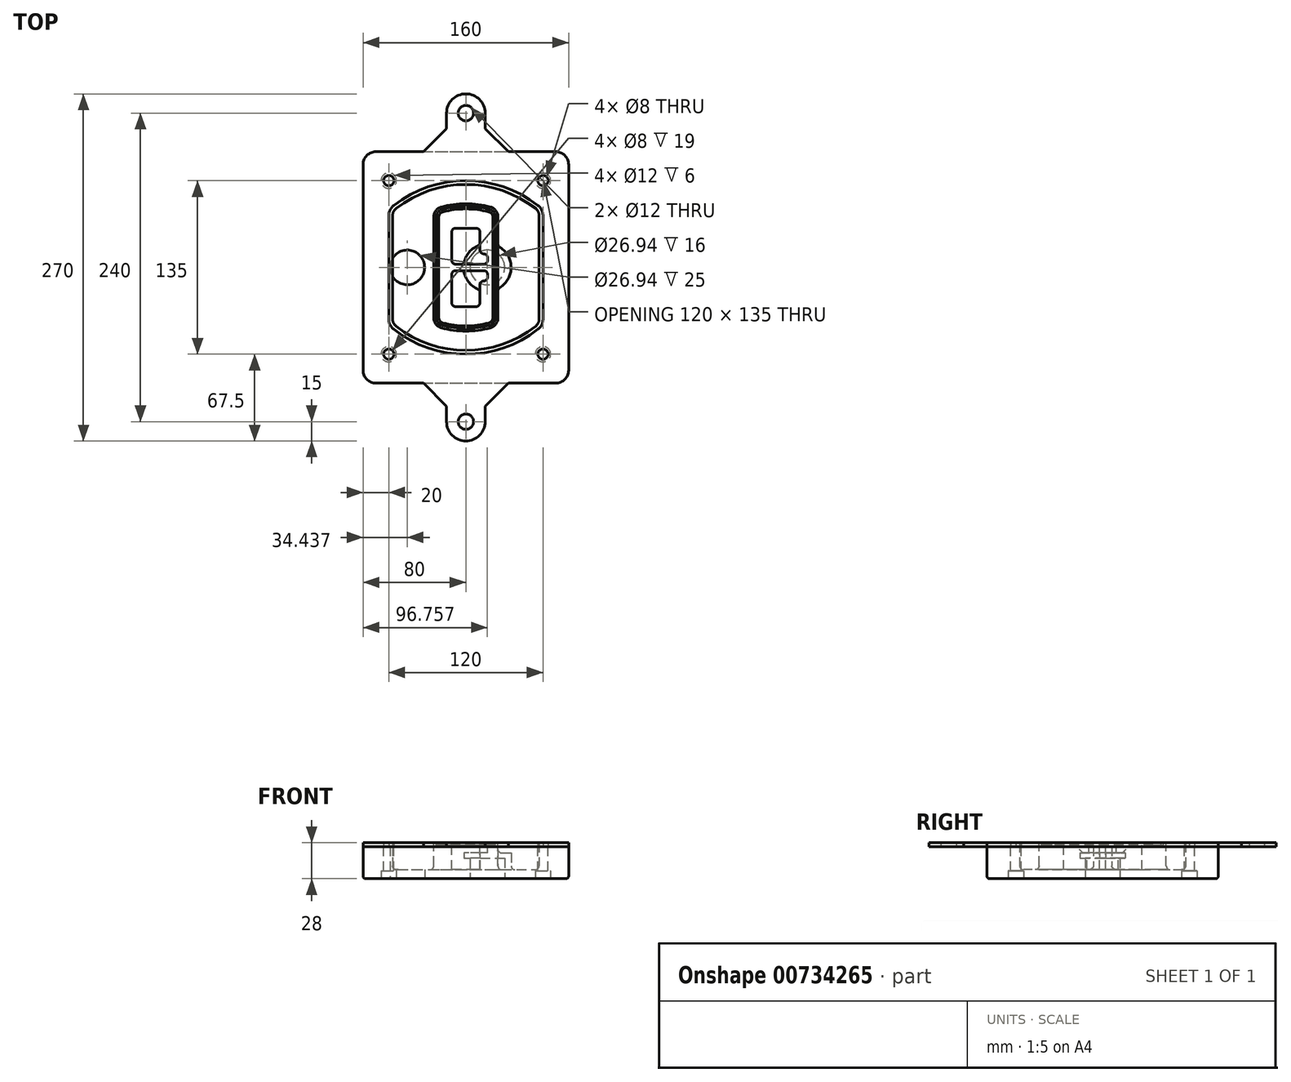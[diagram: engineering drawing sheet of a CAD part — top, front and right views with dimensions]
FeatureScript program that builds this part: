
annotation { "Feature Type Name" : "Feature", "Feature Type Description" : "" }
export const myFeature = defineFeature(function(context is Context, id is Id, definition is map)
    precondition{}
    {
        {
            var Q0;
            Q0=qCreatedBy(makeId("Top.planeOp"),FACE);
            var sketch = newSketch(context, id + "F0", { "sketchPlane" : qUnion([Q0])});
            skPoint(sketch, "E0.rect.middle", {"position": v(0, 0) * mm});
            skLineSegment(sketch, "E1.bottom", {"start": v(-70, -90) * mm, "end": v(70, -90) * mm});
            skLineSegment(sketch, "E1.top", {"start": v(-70, 90) * mm, "end": v(70, 90) * mm});
            skLineSegment(sketch, "E1.left", {"start": v(-80, -80) * mm, "end": v(-80, 80) * mm});
            skLineSegment(sketch, "E1.right", {"start": v(80, -80) * mm, "end": v(80, 80) * mm});
            skLineSegment(sketch, "E2", {"start": v(-80, 90) * mm, "end": v(80, -90) * mm, "construction": true});
            skLineSegment(sketch, "E3", {"start": v(80, 90) * mm, "end": v(-80, -90) * mm, "construction": true});
            skCircle(sketch, "E4", {"center": v(-60, 67.5) * mm, "radius": 4 * mm});
            skCircle(sketch, "E5", {"center": v(60, 67.5) * mm, "radius": 4 * mm});
            skCircle(sketch, "E6", {"center": v(60, -67.5) * mm, "radius": 4 * mm});
            skCircle(sketch, "E7", {"center": v(-60, -67.5) * mm, "radius": 4 * mm});
            skLineSegment(sketch, "E8", {"start": v(-60, 67.5) * mm, "end": v(60, 67.5) * mm, "construction": true});
            skLineSegment(sketch, "E9", {"start": v(60, 67.5) * mm, "end": v(60, -67.5) * mm, "construction": true});
            skLineSegment(sketch, "E10", {"start": v(60, -67.5) * mm, "end": v(-60, -67.5) * mm, "construction": true});
            skLineSegment(sketch, "E11", {"start": v(-60, -67.5) * mm, "end": v(-60, 67.5) * mm, "construction": true});
            skLineSegment(sketch, "E12", {"start": v(-60, 40.3) * mm, "end": v(-60, -40.3) * mm});
            skLineSegment(sketch, "E13", {"start": v(60, 40.3) * mm, "end": v(60, -40.3) * mm});
            skArc(sketch, "E14", {"start": v(56.15, 48.18) * mm, "mid": v(0, 67.5) * mm, "end": v(-56.15, 48.18) * mm});
            skArc(sketch, "E15", {"start": v(-56.15, -48.18) * mm, "mid": v(0, -67.5) * mm, "end": v(56.15, -48.18) * mm});
            skLineSegment(sketch, "E16", {"start": v(-60, 0) * mm, "end": v(60, 0) * mm, "construction": true});
            skPoint(sketch, "E17.visualSharp", {"position": v(-60, -45) * mm});
            skArc(sketch, "E17.filletArc", {"start": v(-60, -40.3) * mm, "mid": v(-58.99, -44.68) * mm, "end": v(-56.15, -48.18) * mm});
            skPoint(sketch, "E18.visualSharp", {"position": v(-60, 45) * mm});
            skArc(sketch, "E18.filletArc", {"start": v(-56.15, 48.18) * mm, "mid": v(-58.99, 44.68) * mm, "end": v(-60, 40.3) * mm});
            skPoint(sketch, "E19.visualSharp", {"position": v(60, 45) * mm});
            skArc(sketch, "E19.filletArc", {"start": v(60, 40.3) * mm, "mid": v(58.99, 44.68) * mm, "end": v(56.15, 48.18) * mm});
            skPoint(sketch, "E20.visualSharp", {"position": v(60, -45) * mm});
            skArc(sketch, "E20.filletArc", {"start": v(56.15, -48.18) * mm, "mid": v(58.99, -44.68) * mm, "end": v(60, -40.3) * mm});
            skPoint(sketch, "E21.visualSharp", {"position": v(-80, 90) * mm});
            skArc(sketch, "E21.filletArc", {"start": v(-70, 90) * mm, "mid": v(-77.07, 87.07) * mm, "end": v(-80, 80) * mm});
            skPoint(sketch, "E22.visualSharp", {"position": v(80, 90) * mm});
            skArc(sketch, "E22.filletArc", {"start": v(80, 80) * mm, "mid": v(77.07, 87.07) * mm, "end": v(70, 90) * mm});
            skPoint(sketch, "E23.visualSharp", {"position": v(80, -90) * mm});
            skArc(sketch, "E23.filletArc", {"start": v(70, -90) * mm, "mid": v(77.07, -87.07) * mm, "end": v(80, -80) * mm});
            skPoint(sketch, "E24.visualSharp", {"position": v(-80, -90) * mm});
            skArc(sketch, "E24.filletArc", {"start": v(-80, -80) * mm, "mid": v(-77.07, -87.07) * mm, "end": v(-70, -90) * mm});
            skArc(sketch, "E25.0", {"start": v(57, 40.3) * mm, "mid": v(56.3, 43.36) * mm, "end": v(54.3, 45.81) * mm});
            skLineSegment(sketch, "E25.1", {"start": v(57, 40.3) * mm, "end": v(57, -40.3) * mm});
            skArc(sketch, "E25.2", {"start": v(54.3, -45.81) * mm, "mid": v(56.3, -43.36) * mm, "end": v(57, -40.3) * mm});
            skArc(sketch, "E25.3", {"start": v(-54.3, -45.81) * mm, "mid": v(0, -64.5) * mm, "end": v(54.3, -45.81) * mm});
            skArc(sketch, "E25.4", {"start": v(-57, -40.3) * mm, "mid": v(-56.3, -43.36) * mm, "end": v(-54.3, -45.81) * mm});
            skArc(sketch, "E25.5", {"start": v(54.3, 45.81) * mm, "mid": v(0, 64.5) * mm, "end": v(-54.3, 45.81) * mm});
            skLineSegment(sketch, "E25.6", {"start": v(-57, 40.3) * mm, "end": v(-57, -40.3) * mm});
            skArc(sketch, "E25.7", {"start": v(-54.3, 45.81) * mm, "mid": v(-56.3, 43.36) * mm, "end": v(-57, 40.3) * mm});
            skArc(sketch, "E26.0", {"start": v(-58.62, 51.33) * mm, "mid": v(-62.58, 46.43) * mm, "end": v(-64, 40.3) * mm});
            skArc(sketch, "E26.1", {"start": v(58.62, 51.33) * mm, "mid": v(0, 71.5) * mm, "end": v(-58.62, 51.33) * mm});
            skArc(sketch, "E26.2", {"start": v(64, 40.3) * mm, "mid": v(62.58, 46.43) * mm, "end": v(58.62, 51.33) * mm});
            skLineSegment(sketch, "E26.3", {"start": v(64, 40.3) * mm, "end": v(64, -40.3) * mm});
            skArc(sketch, "E26.4", {"start": v(58.62, -51.33) * mm, "mid": v(62.58, -46.43) * mm, "end": v(64, -40.3) * mm});
            skLineSegment(sketch, "E26.5", {"start": v(-64, 40.3) * mm, "end": v(-64, -40.3) * mm});
            skArc(sketch, "E26.6", {"start": v(-58.62, -51.33) * mm, "mid": v(0, -71.5) * mm, "end": v(58.62, -51.33) * mm});
            skArc(sketch, "E26.7", {"start": v(-64, -40.3) * mm, "mid": v(-62.58, -46.43) * mm, "end": v(-58.62, -51.33) * mm});
            skSolve(sketch);
        }
        {
            var Q0;
            Q0=makeQuery(id+"F0.imprint","IMPRINT",FACE,{"disambiguationData":[TD([[makeQuery(id+"F0.imprint","IMPRINT",EDGE,{"derivedFrom":sQuery(id+"F0.wireOp",EDGE,"E1.bottom")}),1.0]])]});
            var Q1;
            Q1=makeQuery(id+"F0.imprint","IMPRINT",FACE,{"disambiguationData":[TD([[makeQuery(id+"F0.imprint","IMPRINT",EDGE,{"derivedFrom":sQuery(id+"F0.wireOp",EDGE,"E12")}),1.0]])]});
            var Q2;
            Q2=makeQuery(id+"F0.imprint","IMPRINT",FACE,{"disambiguationData":[TD([[makeQuery(id+"F0.imprint","IMPRINT",EDGE,{"derivedFrom":sQuery(id+"F0.wireOp",EDGE,"E25.0")}),1.0]])]});
            var Q3;
            Q3=makeQuery(id+"F0.imprint","IMPRINT",FACE,{"disambiguationData":[TD([[makeQuery(id+"F0.imprint","IMPRINT",EDGE,{"derivedFrom":sQuery(id+"F0.wireOp",EDGE,"E12")}),-1.0]])]});
            extrude(context, id + "F1", {"entities" : qUnion([Q0, Q1, Q2, Q3]), "oppositeDirection" : true, "depth" : 25 * mm});
        }
        {
            var Q0;
            Q0=makeQuery(id+"F0.imprint","IMPRINT",FACE,{"disambiguationData":[TD([[makeQuery(id+"F0.imprint","IMPRINT",EDGE,{"derivedFrom":sQuery(id+"F0.wireOp",EDGE,"E12")}),1.0]])]});
            extrude(context, id + "F2", {"entities" : qUnion([Q0]), "operationType" : NewBodyOperationType.ADD, "depth" : 3 * mm});
        }
        {
            var Q0;
            Q0=makeQuery(id+"F0.imprint","IMPRINT",FACE,{"disambiguationData":[TD([[makeQuery(id+"F0.imprint","IMPRINT",EDGE,{"derivedFrom":sQuery(id+"F0.wireOp",EDGE,"E25.0")}),1.0]])]});
            extrude(context, id + "F3", {"entities" : qUnion([Q0]), "operationType" : NewBodyOperationType.REMOVE, "oppositeDirection" : true, "depth" : 18 * mm});
        }
        {
            var Q0;
            Q0=makeQuery(id+"F2.opExtrude","CAP_FACE",FACE,{"disambiguationData":[OSD([sQuery(id+"F0.wireOp",EDGE,"E12"),sQuery(id+"F0.wireOp",EDGE,"E13"),sQuery(id+"F0.wireOp",EDGE,"E14"),sQuery(id+"F0.wireOp",EDGE,"E15"),sQuery(id+"F0.wireOp",EDGE,"E17.filletArc"),sQuery(id+"F0.wireOp",EDGE,"E18.filletArc"),sQuery(id+"F0.wireOp",EDGE,"E19.filletArc"),sQuery(id+"F0.wireOp",EDGE,"E20.filletArc"),sQuery(id+"F0.wireOp",EDGE,"E25.0"),sQuery(id+"F0.wireOp",EDGE,"E25.1"),sQuery(id+"F0.wireOp",EDGE,"E25.2"),sQuery(id+"F0.wireOp",EDGE,"E25.3"),sQuery(id+"F0.wireOp",EDGE,"E25.4"),sQuery(id+"F0.wireOp",EDGE,"E25.5"),sQuery(id+"F0.wireOp",EDGE,"E25.6"),sQuery(id+"F0.wireOp",EDGE,"E25.7")])],"isStart":false});
            var sketch = newSketch(context, id + "F4", { "sketchPlane" : qUnion([Q0])});
            skArc(sketch, "E27.0", {"start": v(-19.08, -46.97) * mm, "mid": v(0, -49.5) * mm, "end": v(19.08, -46.97) * mm});
            skArc(sketch, "E28.0", {"start": v(19.08, 46.97) * mm, "mid": v(0, 49.5) * mm, "end": v(-19.08, 46.97) * mm});
            skLineSegment(sketch, "E29", {"start": v(-25, 39.25) * mm, "end": v(-25, -39.25) * mm});
            skLineSegment(sketch, "E30", {"start": v(25, 39.25) * mm, "end": v(25, -39.25) * mm});
            skLineSegment(sketch, "E31", {"start": v(-25, 45.1) * mm, "end": v(25, 45.1) * mm, "construction": true});
            skLineSegment(sketch, "E32", {"start": v(-25, -45.1) * mm, "end": v(25, -45.1) * mm, "construction": true});
            skPoint(sketch, "E33.visualSharp", {"position": v(-25, 45.1) * mm});
            skArc(sketch, "E33.filletArc", {"start": v(-19.08, 46.97) * mm, "mid": v(-23.35, 44.11) * mm, "end": v(-25, 39.25) * mm});
            skPoint(sketch, "E34.visualSharp", {"position": v(25, 45.1) * mm});
            skArc(sketch, "E34.filletArc", {"start": v(25, 39.25) * mm, "mid": v(23.35, 44.11) * mm, "end": v(19.08, 46.97) * mm});
            skPoint(sketch, "E35.visualSharp", {"position": v(25, -45.1) * mm});
            skArc(sketch, "E35.filletArc", {"start": v(19.08, -46.97) * mm, "mid": v(23.35, -44.11) * mm, "end": v(25, -39.25) * mm});
            skPoint(sketch, "E36.visualSharp", {"position": v(-25, -45.1) * mm});
            skArc(sketch, "E36.filletArc", {"start": v(-25, -39.25) * mm, "mid": v(-23.35, -44.11) * mm, "end": v(-19.08, -46.97) * mm});
            skArc(sketch, "E37.0", {"start": v(54.3, 45.81) * mm, "mid": v(0, 64.5) * mm, "end": v(-54.3, 45.81) * mm});
            skArc(sketch, "E37.1", {"start": v(-54.3, 45.81) * mm, "mid": v(-56.3, 43.36) * mm, "end": v(-57, 40.3) * mm});
            skLineSegment(sketch, "E37.2", {"start": v(-57, 40.3) * mm, "end": v(-57, -40.3) * mm});
            skArc(sketch, "E37.3", {"start": v(-57, -40.3) * mm, "mid": v(-56.3, -43.36) * mm, "end": v(-54.3, -45.81) * mm});
            skArc(sketch, "E37.4", {"start": v(-54.3, -45.81) * mm, "mid": v(0, -64.5) * mm, "end": v(54.3, -45.81) * mm});
            skArc(sketch, "E37.5", {"start": v(54.3, -45.81) * mm, "mid": v(56.3, -43.36) * mm, "end": v(57, -40.3) * mm});
            skLineSegment(sketch, "E37.6", {"start": v(57, 40.3) * mm, "end": v(57, -40.3) * mm});
            skArc(sketch, "E37.7", {"start": v(57, 40.3) * mm, "mid": v(56.3, 43.36) * mm, "end": v(54.3, 45.81) * mm});
            skLineSegment(sketch, "E38.0", {"start": v(23, 39.25) * mm, "end": v(23, -39.25) * mm});
            skArc(sketch, "E38.1", {"start": v(18.56, -45.04) * mm, "mid": v(21.76, -42.9) * mm, "end": v(23, -39.25) * mm});
            skArc(sketch, "E38.2", {"start": v(-18.56, -45.04) * mm, "mid": v(0, -47.5) * mm, "end": v(18.56, -45.04) * mm});
            skArc(sketch, "E38.3", {"start": v(-23, -39.25) * mm, "mid": v(-21.76, -42.9) * mm, "end": v(-18.56, -45.04) * mm});
            skLineSegment(sketch, "E38.4", {"start": v(-23, 39.25) * mm, "end": v(-23, -39.25) * mm});
            skArc(sketch, "E38.5", {"start": v(23, 39.25) * mm, "mid": v(21.76, 42.9) * mm, "end": v(18.56, 45.04) * mm});
            skArc(sketch, "E38.6", {"start": v(-18.56, 45.04) * mm, "mid": v(-21.76, 42.9) * mm, "end": v(-23, 39.25) * mm});
            skArc(sketch, "E38.7", {"start": v(18.56, 45.04) * mm, "mid": v(0, 47.5) * mm, "end": v(-18.56, 45.04) * mm});
            skArc(sketch, "E39.0", {"start": v(21, 39.25) * mm, "mid": v(20.18, 41.68) * mm, "end": v(18.04, 43.1) * mm});
            skLineSegment(sketch, "E39.1", {"start": v(21, 39.25) * mm, "end": v(21, -39.25) * mm});
            skArc(sketch, "E39.2", {"start": v(18.04, -43.1) * mm, "mid": v(20.18, -41.68) * mm, "end": v(21, -39.25) * mm});
            skArc(sketch, "E39.3", {"start": v(-18.04, -43.1) * mm, "mid": v(0, -45.5) * mm, "end": v(18.04, -43.1) * mm});
            skArc(sketch, "E39.4", {"start": v(-21, -39.25) * mm, "mid": v(-20.18, -41.68) * mm, "end": v(-18.04, -43.1) * mm});
            skArc(sketch, "E39.5", {"start": v(18.04, 43.1) * mm, "mid": v(0, 45.5) * mm, "end": v(-18.04, 43.1) * mm});
            skLineSegment(sketch, "E39.6", {"start": v(-21, 39.25) * mm, "end": v(-21, -39.25) * mm});
            skArc(sketch, "E39.7", {"start": v(-18.04, 43.1) * mm, "mid": v(-20.18, 41.68) * mm, "end": v(-21, 39.25) * mm});
            skLineSegment(sketch, "E40", {"start": v(-25, 0) * mm, "end": v(25, 0) * mm, "construction": true});
            skLineSegment(sketch, "E41", {"start": v(-11, 5.5) * mm, "end": v(-11, 27.5) * mm});
            skLineSegment(sketch, "E42", {"start": v(-8, 30.5) * mm, "end": v(8, 30.5) * mm});
            skLineSegment(sketch, "E43", {"start": v(11, 27.5) * mm, "end": v(11, 13.5) * mm});
            skLineSegment(sketch, "E44", {"start": v(14, 10.5) * mm, "end": v(14, 10.5) * mm});
            skLineSegment(sketch, "E45", {"start": v(17, 7.5) * mm, "end": v(17, 5.5) * mm});
            skLineSegment(sketch, "E46", {"start": v(14, 2.5) * mm, "end": v(-8, 2.5) * mm});
            skPoint(sketch, "E47.visualSharp", {"position": v(-11, 30.5) * mm});
            skArc(sketch, "E47.filletArc", {"start": v(-8, 30.5) * mm, "mid": v(-10.12, 29.62) * mm, "end": v(-11, 27.5) * mm});
            skPoint(sketch, "E48.visualSharp", {"position": v(11, 30.5) * mm});
            skArc(sketch, "E48.filletArc", {"start": v(11, 27.5) * mm, "mid": v(10.12, 29.62) * mm, "end": v(8, 30.5) * mm});
            skPoint(sketch, "E49.visualSharp", {"position": v(11, 10.5) * mm});
            skArc(sketch, "E49.filletArc", {"start": v(11, 13.5) * mm, "mid": v(11.88, 11.38) * mm, "end": v(14, 10.5) * mm});
            skPoint(sketch, "E50.visualSharp", {"position": v(17, 10.5) * mm});
            skArc(sketch, "E50.filletArc", {"start": v(17, 7.5) * mm, "mid": v(16.12, 9.62) * mm, "end": v(14, 10.5) * mm});
            skPoint(sketch, "E51.visualSharp", {"position": v(17, 2.5) * mm});
            skArc(sketch, "E51.filletArc", {"start": v(14, 2.5) * mm, "mid": v(16.12, 3.38) * mm, "end": v(17, 5.5) * mm});
            skPoint(sketch, "E52.visualSharp", {"position": v(-11, 2.5) * mm});
            skArc(sketch, "E52.filletArc", {"start": v(-11, 5.5) * mm, "mid": v(-10.12, 3.38) * mm, "end": v(-8, 2.5) * mm});
            skLineSegment(sketch, "E53.0.MirrorCS", {"start": v(14, -2.5) * mm, "end": v(-8, -2.5) * mm});
            skArc(sketch, "E54.0.MirrorCS", {"start": v(-11, -5.5) * mm, "mid": v(-10.12, -3.38) * mm, "end": v(-8, -2.5) * mm});
            skLineSegment(sketch, "E55.0.MirrorCS", {"start": v(-11, -5.5) * mm, "end": v(-11, -27.5) * mm});
            skArc(sketch, "E56.0.MirrorCS", {"start": v(-8, -30.5) * mm, "mid": v(-10.12, -29.62) * mm, "end": v(-11, -27.5) * mm});
            skLineSegment(sketch, "E57.0.MirrorCS", {"start": v(-8, -30.5) * mm, "end": v(8, -30.5) * mm});
            skArc(sketch, "E58.0.MirrorCS", {"start": v(11, -27.5) * mm, "mid": v(10.12, -29.62) * mm, "end": v(8, -30.5) * mm});
            skLineSegment(sketch, "E59.0.MirrorCS", {"start": v(11, -27.5) * mm, "end": v(11, -13.5) * mm});
            skArc(sketch, "E60.0.MirrorCS", {"start": v(11, -13.5) * mm, "mid": v(11.88, -11.38) * mm, "end": v(14, -10.5) * mm});
            skArc(sketch, "E61.0.MirrorCS", {"start": v(17, -7.5) * mm, "mid": v(16.12, -9.62) * mm, "end": v(14, -10.5) * mm});
            skLineSegment(sketch, "E62.0.MirrorCS", {"start": v(17, -7.5) * mm, "end": v(17, -5.5) * mm});
            skArc(sketch, "E63.0.MirrorCS", {"start": v(14, -2.5) * mm, "mid": v(16.12, -3.38) * mm, "end": v(17, -5.5) * mm});
            skSolve(sketch);
        }
        {
            var Q0;
            Q0=makeQuery(id+"F4.imprint","IMPRINT",FACE,{"disambiguationData":[TD([[makeQuery(id+"F4.imprint","IMPRINT",EDGE,{"derivedFrom":sQuery(id+"F4.wireOp",EDGE,"E27.0")}),1.0]])]});
            var Q1;
            Q1=makeQuery(id+"F4.imprint","IMPRINT",FACE,{"disambiguationData":[TD([[makeQuery(id+"F4.imprint","IMPRINT",EDGE,{"derivedFrom":sQuery(id+"F4.wireOp",EDGE,"E38.0")}),-1.0]])]});
            var Q2;
            Q2=makeQuery(id+"F4.imprint","IMPRINT",FACE,{"disambiguationData":[TD([[makeQuery(id+"F4.imprint","IMPRINT",EDGE,{"derivedFrom":sQuery(id+"F4.wireOp",EDGE,"E39.0")}),1.0]])]});
            extrude(context, id + "F5", {"entities" : qUnion([Q0, Q1, Q2]), "operationType" : NewBodyOperationType.ADD, "endBound" : BoundingType.UP_TO_NEXT, "oppositeDirection" : true, "depth" : 25 * mm});
        }
        {
            var Q0;
            Q0=makeQuery(id+"F4.imprint","IMPRINT",FACE,{"disambiguationData":[TD([[makeQuery(id+"F4.imprint","IMPRINT",EDGE,{"derivedFrom":sQuery(id+"F4.wireOp",EDGE,"E38.0")}),-1.0]])]});
            extrude(context, id + "F6", {"entities" : qUnion([Q0]), "operationType" : NewBodyOperationType.REMOVE, "oppositeDirection" : true, "depth" : 2 * mm});
        }
        {
            var Q0;
            Q0=makeQuery(id+"F1.opExtrude","CAP_FACE",FACE,{"disambiguationData":[OSD([sQuery(id+"F0.wireOp",EDGE,"E1.bottom"),sQuery(id+"F0.wireOp",EDGE,"E1.top"),sQuery(id+"F0.wireOp",EDGE,"E1.left"),sQuery(id+"F0.wireOp",EDGE,"E1.right"),sQuery(id+"F0.wireOp",EDGE,"E4"),sQuery(id+"F0.wireOp",EDGE,"E5"),sQuery(id+"F0.wireOp",EDGE,"E6"),sQuery(id+"F0.wireOp",EDGE,"E7"),sQuery(id+"F0.wireOp",EDGE,"E21.filletArc"),sQuery(id+"F0.wireOp",EDGE,"E22.filletArc"),sQuery(id+"F0.wireOp",EDGE,"E23.filletArc"),sQuery(id+"F0.wireOp",EDGE,"E24.filletArc")])],"isStart":false});
            var sketch = newSketch(context, id + "F7", { "sketchPlane" : qUnion([Q0])});
            skCircle(sketch, "E64", {"center": v(16.76, 0) * mm, "radius": 13.47 * mm});
            skCircle(sketch, "E65", {"center": v(-45.56, 0) * mm, "radius": 13.47 * mm});
            skLineSegment(sketch, "E66", {"start": v(80, 0) * mm, "end": v(-80, 0) * mm});
            skCircle(sketch, "E67", {"center": v(16.76, 0) * mm, "radius": 18.47 * mm});
            skCircle(sketch, "E68", {"center": v(60, -67.5) * mm, "radius": 6 * mm});
            skCircle(sketch, "E69", {"center": v(-60, -67.5) * mm, "radius": 6 * mm});
            skCircle(sketch, "E70", {"center": v(-60, 67.5) * mm, "radius": 6 * mm});
            skCircle(sketch, "E71", {"center": v(60, 67.5) * mm, "radius": 6 * mm});
            skSolve(sketch);
        }
        {
            var Q0;
            {var subQ1=sQuery(id+"F7.wireOp",EDGE,"E66");var subQ4=sQuery(id+"F7.wireOp",EDGE,"E64");var subQ6=makeQuery(id+"F7.imprint","INTERSECT",VERTEX,{"disambiguationData":[OD(0.0)],"derivedFrom":[subQ4,subQ1]});Q0=makeQuery(id+"F7.imprint","IMPRINT",FACE,{"disambiguationData":[TD([[makeQuery(id+"F7.imprint","IMPRINT",EDGE,{"disambiguationData":[TD([[subQ6,-1.0]])],"derivedFrom":subQ4}),-1.0]])]});}
            var Q1;
            {var subQ0=sQuery(id+"F7.wireOp",EDGE,"E66");var subQ1=sQuery(id+"F7.wireOp",EDGE,"E64");var subQ3=makeQuery(id+"F7.imprint","INTERSECT",VERTEX,{"disambiguationData":[OD(0.0)],"derivedFrom":[subQ1,subQ0]});Q1=makeQuery(id+"F7.imprint","IMPRINT",FACE,{"disambiguationData":[TD([[makeQuery(id+"F7.imprint","IMPRINT",EDGE,{"disambiguationData":[TD([[subQ3,-1.0]])],"derivedFrom":subQ1}),1.0]])]});}
            var Q2;
            {var subQ0=sQuery(id+"F7.wireOp",EDGE,"E66");var subQ1=sQuery(id+"F7.wireOp",EDGE,"E64");var subQ3=makeQuery(id+"F7.imprint","INTERSECT",VERTEX,{"disambiguationData":[OD(0.0)],"derivedFrom":[subQ1,subQ0]});Q2=makeQuery(id+"F7.imprint","IMPRINT",FACE,{"disambiguationData":[TD([[makeQuery(id+"F7.imprint","IMPRINT",EDGE,{"disambiguationData":[TD([[subQ3,1.0]])],"derivedFrom":subQ1}),1.0]])]});}
            var Q3;
            {var subQ1=sQuery(id+"F7.wireOp",EDGE,"E66");var subQ4=sQuery(id+"F7.wireOp",EDGE,"E64");var subQ6=makeQuery(id+"F7.imprint","INTERSECT",VERTEX,{"disambiguationData":[OD(0.0)],"derivedFrom":[subQ4,subQ1]});Q3=makeQuery(id+"F7.imprint","IMPRINT",FACE,{"disambiguationData":[TD([[makeQuery(id+"F7.imprint","IMPRINT",EDGE,{"disambiguationData":[TD([[subQ6,1.0]])],"derivedFrom":subQ4}),-1.0]])]});}
            extrude(context, id + "F8", {"entities" : qUnion([Q0, Q1, Q2, Q3]), "operationType" : NewBodyOperationType.ADD, "oppositeDirection" : true, "depth" : 20 * mm});
        }
        {
            var Q0;
            {var subQ0=sQuery(id+"F7.wireOp",EDGE,"E66");var subQ1=sQuery(id+"F7.wireOp",EDGE,"E64");var subQ3=makeQuery(id+"F7.imprint","INTERSECT",VERTEX,{"disambiguationData":[OD(0.0)],"derivedFrom":[subQ1,subQ0]});Q0=makeQuery(id+"F7.imprint","IMPRINT",FACE,{"disambiguationData":[TD([[makeQuery(id+"F7.imprint","IMPRINT",EDGE,{"disambiguationData":[TD([[subQ3,-1.0]])],"derivedFrom":subQ1}),1.0]])]});}
            var Q1;
            {var subQ0=sQuery(id+"F7.wireOp",EDGE,"E66");var subQ1=sQuery(id+"F7.wireOp",EDGE,"E64");var subQ3=makeQuery(id+"F7.imprint","INTERSECT",VERTEX,{"disambiguationData":[OD(0.0)],"derivedFrom":[subQ1,subQ0]});Q1=makeQuery(id+"F7.imprint","IMPRINT",FACE,{"disambiguationData":[TD([[makeQuery(id+"F7.imprint","IMPRINT",EDGE,{"disambiguationData":[TD([[subQ3,1.0]])],"derivedFrom":subQ1}),1.0]])]});}
            extrude(context, id + "F9", {"entities" : qUnion([Q0, Q1]), "operationType" : NewBodyOperationType.REMOVE, "oppositeDirection" : true, "depth" : 16 * mm});
        }
        {
            var Q0;
            {var subQ0=sQuery(id+"F7.wireOp",EDGE,"E66");var subQ1=sQuery(id+"F7.wireOp",EDGE,"E65");var subQ3=makeQuery(id+"F7.imprint","INTERSECT",VERTEX,{"disambiguationData":[OD(0.0)],"derivedFrom":[subQ1,subQ0]});Q0=makeQuery(id+"F7.imprint","IMPRINT",FACE,{"disambiguationData":[TD([[makeQuery(id+"F7.imprint","IMPRINT",EDGE,{"disambiguationData":[TD([[subQ3,-1.0]])],"derivedFrom":subQ1}),1.0]])]});}
            var Q1;
            {var subQ0=sQuery(id+"F7.wireOp",EDGE,"E66");var subQ1=sQuery(id+"F7.wireOp",EDGE,"E65");var subQ3=makeQuery(id+"F7.imprint","INTERSECT",VERTEX,{"disambiguationData":[OD(0.0)],"derivedFrom":[subQ1,subQ0]});Q1=makeQuery(id+"F7.imprint","IMPRINT",FACE,{"disambiguationData":[TD([[makeQuery(id+"F7.imprint","IMPRINT",EDGE,{"disambiguationData":[TD([[subQ3,1.0]])],"derivedFrom":subQ1}),1.0]])]});}
            extrude(context, id + "F10", {"entities" : qUnion([Q0, Q1]), "operationType" : NewBodyOperationType.REMOVE, "oppositeDirection" : true, "depth" : 25 * mm});
        }
        {
            var Q0;
            Q0=makeQuery(id+"F7.imprint","IMPRINT",FACE,{"disambiguationData":[TD([[makeQuery(id+"F7.imprint","IMPRINT",EDGE,{"derivedFrom":sQuery(id+"F7.wireOp",EDGE,"E68")}),1.0]])]});
            var Q1;
            Q1=makeQuery(id+"F7.imprint","IMPRINT",FACE,{"disambiguationData":[TD([[makeQuery(id+"F7.imprint","IMPRINT",EDGE,{"derivedFrom":makeQuery(id+"F1.opExtrude","CAP_EDGE",EDGE,{"disambiguationData":[OSD([sQuery(id+"F0.wireOp",EDGE,"E5")])],"isStart":false})}),-1.0]])]});
            var Q2;
            Q2=makeQuery(id+"F7.imprint","IMPRINT",FACE,{"disambiguationData":[TD([[makeQuery(id+"F7.imprint","IMPRINT",EDGE,{"derivedFrom":sQuery(id+"F7.wireOp",EDGE,"E69")}),1.0]])]});
            var Q3;
            Q3=makeQuery(id+"F7.imprint","IMPRINT",FACE,{"disambiguationData":[TD([[makeQuery(id+"F7.imprint","IMPRINT",EDGE,{"derivedFrom":makeQuery(id+"F1.opExtrude","CAP_EDGE",EDGE,{"disambiguationData":[OSD([sQuery(id+"F0.wireOp",EDGE,"E4")])],"isStart":false})}),-1.0]])]});
            var Q4;
            Q4=makeQuery(id+"F7.imprint","IMPRINT",FACE,{"disambiguationData":[TD([[makeQuery(id+"F7.imprint","IMPRINT",EDGE,{"derivedFrom":sQuery(id+"F7.wireOp",EDGE,"E70")}),1.0]])]});
            var Q5;
            Q5=makeQuery(id+"F7.imprint","IMPRINT",FACE,{"disambiguationData":[TD([[makeQuery(id+"F7.imprint","IMPRINT",EDGE,{"derivedFrom":makeQuery(id+"F1.opExtrude","CAP_EDGE",EDGE,{"disambiguationData":[OSD([sQuery(id+"F0.wireOp",EDGE,"E7")])],"isStart":false})}),-1.0]])]});
            var Q6;
            Q6=makeQuery(id+"F7.imprint","IMPRINT",FACE,{"disambiguationData":[TD([[makeQuery(id+"F7.imprint","IMPRINT",EDGE,{"derivedFrom":sQuery(id+"F7.wireOp",EDGE,"E71")}),1.0]])]});
            var Q7;
            Q7=makeQuery(id+"F7.imprint","IMPRINT",FACE,{"disambiguationData":[TD([[makeQuery(id+"F7.imprint","IMPRINT",EDGE,{"derivedFrom":makeQuery(id+"F1.opExtrude","CAP_EDGE",EDGE,{"disambiguationData":[OSD([sQuery(id+"F0.wireOp",EDGE,"E6")])],"isStart":false})}),-1.0]])]});
            extrude(context, id + "F11", {"entities" : qUnion([Q0, Q1, Q2, Q3, Q4, Q5, Q6, Q7]), "operationType" : NewBodyOperationType.REMOVE, "oppositeDirection" : true, "depth" : 6 * mm});
        }
        {
            var Q0;
            Q0=makeQuery(id+"F9.boolean.opBoolean","COPY",FACE,{"derivedFrom":makeQuery(id+"F9.opExtrude","CAP_FACE",FACE,{"disambiguationData":[OSD([sQuery(id+"F7.wireOp",EDGE,"E64")])],"isStart":false})});
            var sketch = newSketch(context, id + "F12", { "sketchPlane" : qUnion([Q0])});
            skArc(sketch, "E72.0", {"start": v(11, 17.55) * mm, "mid": v(2.57, 11.82) * mm, "end": v(-1.54, 2.5) * mm});
            skArc(sketch, "E72.1", {"start": v(-1.54, -2.5) * mm, "mid": v(2.57, -11.82) * mm, "end": v(11, -17.55) * mm});
            skLineSegment(sketch, "E73", {"start": v(-1.54, -2.5) * mm, "end": v(14, -2.5) * mm});
            skLineSegment(sketch, "E74.0", {"start": v(14, 2.5) * mm, "end": v(-1.54, 2.5) * mm});
            skArc(sketch, "E74.1", {"start": v(14, 2.5) * mm, "mid": v(16.12, 3.38) * mm, "end": v(17, 5.5) * mm});
            skLineSegment(sketch, "E74.2", {"start": v(17, 7.5) * mm, "end": v(17, 5.5) * mm});
            skArc(sketch, "E74.3", {"start": v(17, 7.5) * mm, "mid": v(16.12, 9.62) * mm, "end": v(14, 10.5) * mm});
            skArc(sketch, "E74.4", {"start": v(11, 13.5) * mm, "mid": v(11.88, 11.38) * mm, "end": v(14, 10.5) * mm});
            skLineSegment(sketch, "E74.5", {"start": v(11, 17.55) * mm, "end": v(11, 13.5) * mm});
            skLineSegment(sketch, "E74.7", {"start": v(14, -2.5) * mm, "end": v(-1.54, -2.5) * mm});
            skArc(sketch, "E74.8", {"start": v(14, -2.5) * mm, "mid": v(16.12, -3.38) * mm, "end": v(17, -5.5) * mm});
            skLineSegment(sketch, "E74.9", {"start": v(17, -7.5) * mm, "end": v(17, -5.5) * mm});
            skArc(sketch, "E74.10", {"start": v(17, -7.5) * mm, "mid": v(16.12, -9.62) * mm, "end": v(14, -10.5) * mm});
            skArc(sketch, "E74.11", {"start": v(11, -13.5) * mm, "mid": v(11.88, -11.38) * mm, "end": v(14, -10.5) * mm});
            skLineSegment(sketch, "E74.12", {"start": v(11, -17.55) * mm, "end": v(11, -13.5) * mm});
            skPoint(sketch, "E75.orphan", {"position": v(11, -27.5) * mm});
            skPoint(sketch, "E76.orphan", {"position": v(-8, -2.5) * mm});
            skPoint(sketch, "E77.orphan", {"position": v(-8, 2.5) * mm});
            skPoint(sketch, "E78.orphan", {"position": v(11, 27.5) * mm});
            skSolve(sketch);
        }
        {
            var Q0;
            {var subQ7=sQuery(id+"F12.wireOp",EDGE,"E72.0");var subQ14=sQuery(id+"F12.wireOp",EDGE,"E72.1");var subQ16=sQuery(id+"F12.wireOp",EDGE,"E74.1");var subQ18=sQuery(id+"F12.wireOp",EDGE,"E74.8");Q0=qUnion([makeQuery(id+"F12.imprint","IMPRINT",FACE,{"disambiguationData":[TD([[makeQuery(id+"F12.imprint","IMPRINT",EDGE,{"derivedFrom":subQ7}),1.0]])]}),makeQuery(id+"F12.imprint","IMPRINT",FACE,{"disambiguationData":[TD([[makeQuery(id+"F12.imprint","IMPRINT",EDGE,{"derivedFrom":subQ14}),1.0]])]}),makeQuery(id+"F12.imprint","IMPRINT",FACE,{"disambiguationData":[TD([[makeQuery(id+"F12.imprint","IMPRINT",EDGE,{"derivedFrom":subQ16}),1.0]])]}),makeQuery(id+"F12.imprint","IMPRINT",FACE,{"disambiguationData":[TD([[makeQuery(id+"F12.imprint","IMPRINT",EDGE,{"derivedFrom":subQ18}),-1.0]])]})]);}
            var Q1;
            Q1=makeQuery(id+"F5.boolean.opBoolean","SPLIT",FACE,{"disambiguationData":[TD([makeQuery(id+"F5.opExtrude","SWEPT_FACE",FACE,{"disambiguationData":[OSD([sQuery(id+"F4.wireOp",EDGE,"E41")])]})])],"derivedFrom":makeQuery(id+"F3.boolean.opBoolean","COPY",FACE,{"derivedFrom":makeQuery(id+"F3.opExtrude","CAP_FACE",FACE,{"disambiguationData":[OSD([sQuery(id+"F0.wireOp",EDGE,"E25.0"),sQuery(id+"F0.wireOp",EDGE,"E25.1"),sQuery(id+"F0.wireOp",EDGE,"E25.2"),sQuery(id+"F0.wireOp",EDGE,"E25.3"),sQuery(id+"F0.wireOp",EDGE,"E25.4"),sQuery(id+"F0.wireOp",EDGE,"E25.5"),sQuery(id+"F0.wireOp",EDGE,"E25.6"),sQuery(id+"F0.wireOp",EDGE,"E25.7")])],"isStart":false})})});
            extrude(context, id + "F13", {"entities" : qUnion([Q0]), "operationType" : NewBodyOperationType.REMOVE, "endBound" : BoundingType.UP_TO_SURFACE, "endBoundEntityFace" : qUnion([Q1]), "depth" : 25 * mm});
        }
        {
            var Q0;
            Q0=makeQuery(id+"F3.boolean.opBoolean","COPY",EDGE,{"derivedFrom":makeQuery(id+"F3.opExtrude","CAP_EDGE",EDGE,{"disambiguationData":[OSD([sQuery(id+"F0.wireOp",EDGE,"E25.6")])],"isStart":false})});
            var Q1;
            Q1=makeQuery(id+"F8.boolean.opBoolean","INTERSECT",EDGE,{"derivedFrom":[makeQuery(id+"F5.opExtrude","SWEPT_FACE",FACE,{"disambiguationData":[OSD([sQuery(id+"F4.wireOp",EDGE,"E30")])]}),makeQuery(id+"F8.opExtrude","CAP_FACE",FACE,{"disambiguationData":[OSD([sQuery(id+"F7.wireOp",EDGE,"E67")])],"isStart":false})]});
            var Q2;
            Q2=makeQuery(id+"F8.boolean.opBoolean","INTERSECT",EDGE,{"disambiguationData":[OD(1.0)],"derivedFrom":[makeQuery(id+"F5.opExtrude","SWEPT_FACE",FACE,{"disambiguationData":[OSD([sQuery(id+"F4.wireOp",EDGE,"E30")])]}),makeQuery(id+"F8.opExtrude","SWEPT_FACE",FACE,{"disambiguationData":[OSD([sQuery(id+"F7.wireOp",EDGE,"E67")])]})]});
            var Q3;
            {var subQ0=sQuery(id+"F4.wireOp",EDGE,"E30");Q3=makeQuery(id+"F8.boolean.opBoolean","SPLIT",EDGE,{"disambiguationData":[TD([makeQuery(id+"F5.opExtrude","SWEPT_FACE",FACE,{"disambiguationData":[OSD([sQuery(id+"F4.wireOp",EDGE,"E35.filletArc")])]})])],"derivedFrom":makeQuery(id+"F5.opExtrude","CAP_EDGE",EDGE,{"disambiguationData":[OSD([subQ0])],"isStart":false})});}
            var Q4;
            {var subQ0=sQuery(id+"F0.wireOp",EDGE,"E25.7");var subQ1=sQuery(id+"F0.wireOp",EDGE,"E25.1");var subQ2=sQuery(id+"F0.wireOp",EDGE,"E25.6");var subQ3=sQuery(id+"F0.wireOp",EDGE,"E25.5");var subQ4=sQuery(id+"F0.wireOp",EDGE,"E25.4");var subQ5=sQuery(id+"F0.wireOp",EDGE,"E25.0");var subQ6=sQuery(id+"F0.wireOp",EDGE,"E25.2");var subQ7=sQuery(id+"F0.wireOp",EDGE,"E25.3");Q4=makeQuery(id+"F8.boolean.opBoolean","INTERSECT",EDGE,{"derivedFrom":[makeQuery(id+"F5.boolean.opBoolean","SPLIT",FACE,{"disambiguationData":[TD([makeQuery(id+"F2.opExtrude","SWEPT_FACE",FACE,{"disambiguationData":[OSD([subQ5])]})])],"derivedFrom":makeQuery(id+"F3.boolean.opBoolean","COPY",FACE,{"derivedFrom":makeQuery(id+"F3.opExtrude","CAP_FACE",FACE,{"disambiguationData":[OSD([subQ5,subQ1,subQ6,subQ7,subQ4,subQ3,subQ2,subQ0])],"isStart":false})})}),makeQuery(id+"F8.opExtrude","SWEPT_FACE",FACE,{"disambiguationData":[OSD([sQuery(id+"F7.wireOp",EDGE,"E67")])]})]});}
            var Q5;
            Q5=makeQuery(id+"F8.boolean.opBoolean","INTERSECT",EDGE,{"disambiguationData":[OD(0.0)],"derivedFrom":[makeQuery(id+"F5.opExtrude","SWEPT_FACE",FACE,{"disambiguationData":[OSD([sQuery(id+"F4.wireOp",EDGE,"E30")])]}),makeQuery(id+"F8.opExtrude","SWEPT_FACE",FACE,{"disambiguationData":[OSD([sQuery(id+"F7.wireOp",EDGE,"E67")])]})]});
            fillet(context, id + "F14", {"entities" : qUnion([Q0, Q1, Q2, Q3, Q4, Q5]), "radius" : 3 * mm, "tangentPropagation" : true, "allowEdgeOverflow" : false});
        }
        {
            var Q0;
            Q0=makeQuery(id+"F1.opExtrude","CAP_EDGE",EDGE,{"disambiguationData":[OSD([sQuery(id+"F0.wireOp",EDGE,"E1.bottom")])],"isStart":false});
            fillet(context, id + "F15", {"entities" : qUnion([Q0]), "radius" : 2 * mm, "tangentPropagation" : true, "allowEdgeOverflow" : false});
        }
        {
            var Q0;
            {var subQ0=sQuery(id+"F0.wireOp",EDGE,"E21.filletArc");var subQ1=sQuery(id+"F0.wireOp",EDGE,"E7");var subQ2=sQuery(id+"F0.wireOp",EDGE,"E6");var subQ3=sQuery(id+"F0.wireOp",EDGE,"E5");var subQ4=sQuery(id+"F0.wireOp",EDGE,"E4");var subQ5=sQuery(id+"F0.wireOp",EDGE,"E22.filletArc");var subQ6=sQuery(id+"F0.wireOp",EDGE,"E1.bottom");var subQ7=sQuery(id+"F0.wireOp",EDGE,"E1.right");var subQ8=sQuery(id+"F0.wireOp",EDGE,"E1.top");var subQ9=sQuery(id+"F0.wireOp",EDGE,"E1.left");var subQ10=sQuery(id+"F0.wireOp",EDGE,"E23.filletArc");var subQ11=sQuery(id+"F0.wireOp",EDGE,"E24.filletArc");Q0=makeQuery(id+"F2.boolean.opBoolean","SPLIT",FACE,{"disambiguationData":[TD([makeQuery(id+"F1.opExtrude","SWEPT_FACE",FACE,{"disambiguationData":[OSD([subQ6])]})])],"derivedFrom":makeQuery(id+"F1.opExtrude","CAP_FACE",FACE,{"disambiguationData":[OSD([subQ6,subQ8,subQ9,subQ7,subQ4,subQ3,subQ2,subQ1,subQ0,subQ5,subQ10,subQ11])],"isStart":true})});}
            var sketch = newSketch(context, id + "F16", { "sketchPlane" : qUnion([Q0])});
            skLineSegment(sketch, "E79", {"start": v(-33, 90) * mm, "end": v(-15, 108) * mm});
            skLineSegment(sketch, "E80", {"start": v(-15, 108) * mm, "end": v(-15, 120) * mm});
            skLineSegment(sketch, "E81", {"start": v(33, 90) * mm, "end": v(15, 108) * mm});
            skLineSegment(sketch, "E82", {"start": v(15, 108) * mm, "end": v(15, 120) * mm});
            skArc(sketch, "E83", {"start": v(15, 120) * mm, "mid": v(0, 135) * mm, "end": v(-15, 120) * mm});
            skLineSegment(sketch, "E84", {"start": v(-80, 0) * mm, "end": v(80, 0) * mm, "construction": true});
            skLineSegment(sketch, "E85", {"start": v(0, 120) * mm, "end": v(0, 90) * mm, "construction": true});
            skCircle(sketch, "E86", {"center": v(0, 120) * mm, "radius": 6 * mm});
            skLineSegment(sketch, "E87.MirrorCS", {"start": v(-33, -90) * mm, "end": v(-15, -108) * mm});
            skLineSegment(sketch, "E88.MirrorCS", {"start": v(0, -120) * mm, "end": v(0, -90) * mm, "construction": true});
            skCircle(sketch, "E89.MirrorC", {"center": v(0, -120) * mm, "radius": 6 * mm});
            skLineSegment(sketch, "E90.MirrorCS", {"start": v(-15, -108) * mm, "end": v(-15, -120) * mm});
            skArc(sketch, "E91.MirrorCS", {"start": v(15, -120) * mm, "mid": v(0, -135) * mm, "end": v(-15, -120) * mm});
            skLineSegment(sketch, "E92.MirrorCS", {"start": v(15, -108) * mm, "end": v(15, -120) * mm});
            skLineSegment(sketch, "E93.MirrorCS", {"start": v(33, -90) * mm, "end": v(15, -108) * mm});
            skSolve(sketch);
        }
        {
            var Q0;
            {var subQ1=sQuery(id+"F16.wireOp",EDGE,"E79");Q0=makeQuery(id+"F16.imprint","IMPRINT",FACE,{"disambiguationData":[TD([[makeQuery(id+"F16.imprint","IMPRINT",EDGE,{"derivedFrom":subQ1}),-1.0]])]});}
            var Q1;
            Q1=makeQuery(id+"F16.imprint","IMPRINT",FACE,{"disambiguationData":[TD([[makeQuery(id+"F16.imprint","IMPRINT",EDGE,{"derivedFrom":makeQuery(id+"F1.opExtrude","CAP_EDGE",EDGE,{"disambiguationData":[OSD([sQuery(id+"F0.wireOp",EDGE,"E1.left")])],"isStart":true})}),-1.0]])]});
            var Q2;
            {var subQ0=sQuery(id+"F16.wireOp",EDGE,"E87.MirrorCS");Q2=makeQuery(id+"F16.imprint","IMPRINT",FACE,{"disambiguationData":[TD([[makeQuery(id+"F16.imprint","IMPRINT",EDGE,{"derivedFrom":subQ0}),1.0]])]});}
            var Q3;
            Q3=makeQuery(id+"F2.opExtrude","CAP_FACE",FACE,{"disambiguationData":[OSD([sQuery(id+"F0.wireOp",EDGE,"E12"),sQuery(id+"F0.wireOp",EDGE,"E13"),sQuery(id+"F0.wireOp",EDGE,"E14"),sQuery(id+"F0.wireOp",EDGE,"E15"),sQuery(id+"F0.wireOp",EDGE,"E17.filletArc"),sQuery(id+"F0.wireOp",EDGE,"E18.filletArc"),sQuery(id+"F0.wireOp",EDGE,"E19.filletArc"),sQuery(id+"F0.wireOp",EDGE,"E20.filletArc"),sQuery(id+"F0.wireOp",EDGE,"E25.0"),sQuery(id+"F0.wireOp",EDGE,"E25.1"),sQuery(id+"F0.wireOp",EDGE,"E25.2"),sQuery(id+"F0.wireOp",EDGE,"E25.3"),sQuery(id+"F0.wireOp",EDGE,"E25.4"),sQuery(id+"F0.wireOp",EDGE,"E25.5"),sQuery(id+"F0.wireOp",EDGE,"E25.6"),sQuery(id+"F0.wireOp",EDGE,"E25.7")])],"isStart":false});
            extrude(context, id + "F17", {"entities" : qUnion([Q0, Q1, Q2]), "endBound" : BoundingType.UP_TO_SURFACE, "depth" : 25 * mm, "endBoundEntityFace" : qUnion([Q3]), "offsetDistance" : 25 * mm});
        }
    });
